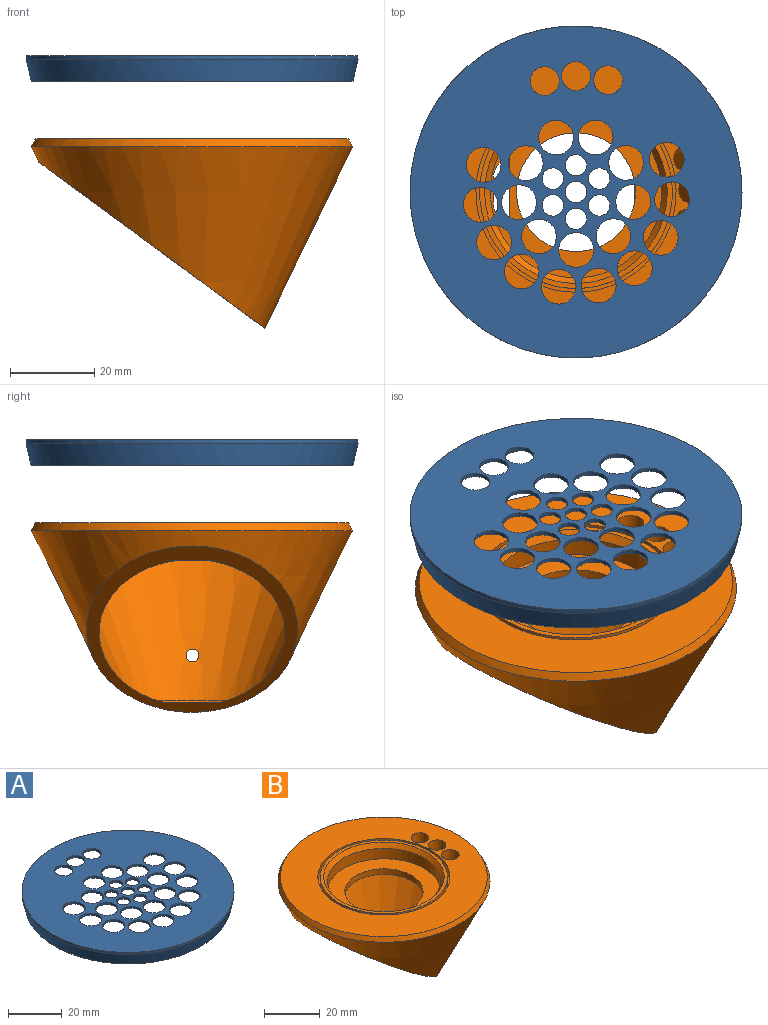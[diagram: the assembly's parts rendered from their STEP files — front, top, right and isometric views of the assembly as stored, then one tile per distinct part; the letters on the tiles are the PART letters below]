
ASSEMBLY  parts=2 mates=1
PART A: 38 faces, bbox 82x82x6 mm
  f0: plane 74.85x74.85mm, normal (0,0,-1), area 3130.6mm2, adj f3,f4,f5,f6,f7,f8,f9,f10
  f1: cylinder r=39.37mm len=78.74mm, axis (0,0,-1), area 236.5mm2, adj f2,f34
  f2: plane 78.74x78.74mm, normal (0,0,1), area 3599.7mm2, adj f1,f3,f4,f5,f6,f7,f8,f9
  f3: cylinder r=4.13mm len=8.26mm, axis (0,0,1), area 24.8mm2, adj f0,f2
  f4: cylinder r=2.54mm len=5.08mm, axis (0,0,1), area 15.3mm2, adj f0,f2
  f5: cylinder r=2.54mm len=5.08mm, axis (0,0,1), area 15.3mm2, adj f0,f2
  f6: cylinder r=2.54mm len=5.08mm, axis (0,0,1), area 15.3mm2, adj f0,f2
  f7: cylinder r=2.54mm len=5.08mm, axis (0,0,1), area 15.3mm2, adj f0,f2
  f8: cylinder r=4.13mm len=8.26mm, axis (0,0,1), area 24.8mm2, adj f0,f2
  f9: cylinder r=4.13mm len=8.26mm, axis (0,0,1), area 24.8mm2, adj f0,f2
  f10: cylinder r=2.54mm len=5.08mm, axis (0,0,1), area 15.3mm2, adj f0,f2
  f11: cylinder r=2.54mm len=5.08mm, axis (0,0,1), area 15.3mm2, adj f0,f2
  f12: cylinder r=3.43mm len=6.86mm, axis (0,0,1), area 20.6mm2, adj f0,f2
  f13: cylinder r=3.43mm len=6.86mm, axis (0,0,1), area 20.6mm2, adj f0,f2
  f14: cylinder r=3.43mm len=6.86mm, axis (0,0,1), area 20.6mm2, adj f0,f2
  f15: cylinder r=2.55mm len=5.1mm, axis (0,0,1), area 15.3mm2, adj f0,f2
  f16: cylinder r=4.13mm len=8.26mm, axis (0,0,1), area 24.8mm2, adj f0,f2
  f17: cylinder r=4.13mm len=8.26mm, axis (0,0,1), area 24.8mm2, adj f0,f2
  f18: cylinder r=4.13mm len=8.26mm, axis (0,0,1), area 24.8mm2, adj f0,f2
  f19: cylinder r=4.13mm len=8.26mm, axis (0,0,1), area 24.8mm2, adj f0,f2
  f20: cylinder r=4.13mm len=8.26mm, axis (0,0,1), area 24.8mm2, adj f0,f2
  f21: cylinder r=4.13mm len=8.26mm, axis (0,0,1), area 24.8mm2, adj f0,f2
  f22: cylinder r=4.13mm len=8.26mm, axis (0,0,1), area 24.8mm2, adj f0,f2
  f23: cylinder r=4.13mm len=8.26mm, axis (0,0,1), area 24.8mm2, adj f0,f2
  f24: cylinder r=4.13mm len=8.26mm, axis (0,0,1), area 24.8mm2, adj f0,f2
  f25: cylinder r=4.13mm len=8.26mm, axis (0,0,1), area 24.8mm2, adj f0,f2
  f26: cylinder r=4.13mm len=8.26mm, axis (0,0,1), area 24.8mm2, adj f0,f2
  f27: cylinder r=4.13mm len=8.26mm, axis (0,0,1), area 24.8mm2, adj f0,f2
  f28: cylinder r=4.13mm len=8.26mm, axis (0,0,1), area 24.8mm2, adj f0,f2
  f29: cylinder r=4.13mm len=8.26mm, axis (0,0,1), area 24.8mm2, adj f0,f2
  f30: cylinder r=4.13mm len=8.26mm, axis (0,0,1), area 24.8mm2, adj f0,f2
  f31: cylinder r=4.13mm len=8.26mm, axis (0,0,1), area 24.8mm2, adj f0,f2
  f32: cone r=38.06mm half-angle=13deg, axis (0,0,1), area 924.3mm2, adj f33,f37
  f33: plane 76.39x76.39mm, normal (0,0,-1), area 240.6mm2, adj f32,f34
  f34: cone r=38.2mm half-angle=13deg, axis (0,0,1), area 1270.5mm2, adj f1,f33
  f35: cylinder r=37.43mm len=74.85mm, axis (0,0,1), area 238.9mm2, adj f0,f36
  f36: torus R=37.68mm, axis (0,0,1), area 94.1mm2, adj f35,f37
  f37: plane 76.12x76.12mm, normal (0,0,-1), area 90.7mm2, adj f32,f36
PART B: 26 faces, bbox 76.2x76.2x45.2 mm
  f0: cone r=31.87mm half-angle=25.8deg, axis (0,0,1), area 3559.3mm2, adj f3,f4,f24,f25
  f1: cone r=38.1mm half-angle=25.8deg, axis (0,0,1), area 5618.2mm2, adj f11,f24,f25
  f2: plane 12.47x1.33mm, normal (0,0,1), area 11.1mm2, adj f3,f24
  f3: torus R=15.31mm, axis (0,0,-1), area 8.4mm2, adj f0,f2,f24
  f4: plane 63.75x63.57mm, normal (0,0,-1), area 2420mm2, adj f0,f6,f12,f13,f14,f15,f16,f17
  f5: plane 45.72x45.72mm, normal (0,0,1), area 169.4mm2, adj f9,f21
  f6: cylinder r=14.09mm len=28.19mm, axis (0,0,-1), area 218.4mm2, adj f4,f7
  f7: plane 40.64x40.64mm, normal (0,0,1), area 621.1mm2, adj f6,f8,f12,f13,f14,f15,f16,f17
  f8: cylinder r=20.32mm len=40.64mm, axis (0,0,-1), area 583.7mm2, adj f7,f9
  f9: cone r=21.65mm half-angle=35.5deg, axis (0,0,1), area 301.8mm2, adj f5,f8
  f10: plane 74.35x74.35mm, normal (0,0,1), area 2475mm2, adj f11,f18,f19,f20,f22
  f11: cone r=38.1mm half-angle=26.4deg, axis (0,0,-1), area 492mm2, adj f1,f10
  f12: plane 5.72x2.47mm, normal (1,0,0), area 14.1mm2, adj f4,f7,f13,f17
  f13: cylinder r=5.08mm len=4.76mm, axis (0,0,1), area 15.2mm2, adj f4,f7,f12,f14
  f14: cylinder r=0.51mm len=2.47mm, axis (0,0,1), area 2.4mm2, adj f4,f7,f13,f15
  f15: plane 14.28x2.47mm, normal (-1,0,0), area 35.2mm2, adj f4,f7,f14,f16
  f16: cylinder r=0.51mm len=2.47mm, axis (0,0,1), area 2.4mm2, adj f4,f7,f15,f17
  f17: cylinder r=5.08mm len=4.76mm, axis (0,0,1), area 15.2mm2, adj f4,f7,f12,f16
  f18: cylinder r=3.17mm len=8.9mm, axis (0,0,1), area 177.6mm2, adj f4,f10
  f19: cylinder r=3.17mm len=8.9mm, axis (0,0,1), area 177.6mm2, adj f4,f10
  f20: cylinder r=3.17mm len=8.9mm, axis (0,0,1), area 177.6mm2, adj f4,f10
  f21: cylinder r=22.86mm len=45.72mm, axis (0,0,1), area 364.8mm2, adj f5,f23
  f22: cylinder r=23.75mm len=47.5mm, axis (0,0,1), area 379mm2, adj f10,f23
  f23: plane 47.5x47.5mm, normal (0,0,1), area 130.2mm2, adj f21,f22
  f24: plane 53.67x50.16mm, normal (-0.59,0,-0.81), area 609.1mm2, adj f0,f1,f2,f3,f4
  f25: cylinder r=1.52mm len=4.3mm, axis (1,0,0), area 27mm2, adj f0,f1
PLACE A t=(21.56,-11.69,58.87)mm
PLACE B t=(21.56,-18.84,-10.7)mm
MATE slider A.f15 <-> B.f9  axis (0,0,1) through (21.56,-11.69,63.64)mm
